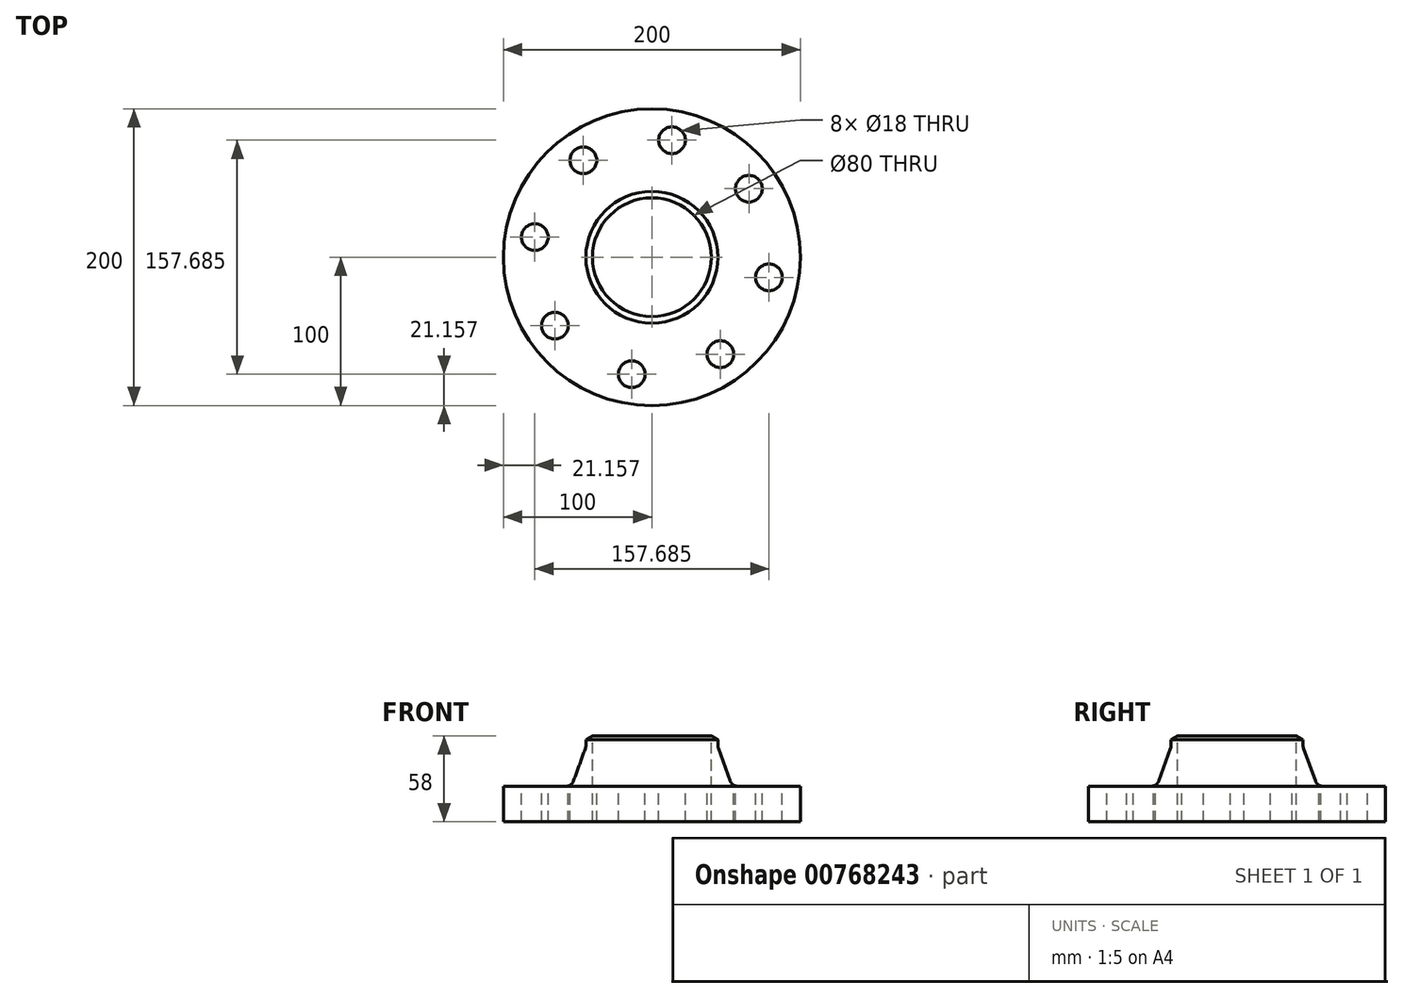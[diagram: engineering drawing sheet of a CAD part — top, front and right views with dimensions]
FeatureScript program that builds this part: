
annotation { "Feature Type Name" : "Feature", "Feature Type Description" : "" }
export const myFeature = defineFeature(function(context is Context, id is Id, definition is map)
    precondition{}
    {
        {
            var Q0;
            Q0=qCreatedBy(makeId("Front.planeOp"),FACE);
            var sketch = newSketch(context, id + "F0", { "sketchPlane" : qUnion([Q0])});
            skLineSegment(sketch, "E0", {"start": v(0, 94.05) * mm, "end": v(0, -88.04) * mm, "construction": true});
            skLineSegment(sketch, "E1", {"start": v(-40, 0) * mm, "end": v(-40, 58) * mm});
            skLineSegment(sketch, "E2", {"start": v(-40, 58) * mm, "end": v(-44.45, 55.43) * mm});
            skLineSegment(sketch, "E3", {"start": v(-54.07, 24) * mm, "end": v(-100, 24) * mm});
            skLineSegment(sketch, "E4", {"start": v(-100, 24) * mm, "end": v(-100, 0) * mm});
            skLineSegment(sketch, "E5", {"start": v(-100, 0) * mm, "end": v(-40, 0) * mm});
            skLineSegment(sketch, "E6", {"start": v(-44.45, 55.43) * mm, "end": v(-44.45, 50.43) * mm});
            skLineSegment(sketch, "E7", {"start": v(-44.45, 50.43) * mm, "end": v(-54.07, 24) * mm});
            skSolve(sketch);
        }
        {
            var Q0;
            Q0=makeQuery(id+"F0.imprint","IMPRINT",FACE,{"disambiguationData":[TD([[makeQuery(id+"F0.imprint","IMPRINT",EDGE,{"derivedFrom":sQuery(id+"F0.wireOp",EDGE,"E1")}),1.0]])]});
            var Q1;
            Q1=sQuery(id+"F0.wireOp",EDGE,"E0");
            revolve(context, id + "F1", {"surfaceOperationType" : NewSurfaceOperationType.NEW, "entities" : qUnion([Q0]), "axis" : qUnion([Q1]), "revolveType" : RevolveType.FULL});
        }
        {
            var Q0;
            Q0=makeQuery(id+"F1.opRevolve","SWEPT_FACE",FACE,{"disambiguationData":[OSD([sQuery(id+"F0.wireOp",EDGE,"E3")])]});
            var sketch = newSketch(context, id + "F2", { "sketchPlane" : qUnion([Q0])});
            skCircle(sketch, "E8", {"center": v(0, 0) * mm, "radius": 80 * mm, "construction": true});
            skCircle(sketch, "E9", {"center": v(-46.16, 65.34) * mm, "radius": 9 * mm});
            skCircle(sketch, "E10.1.0", {"center": v(-78.84, 13.56) * mm, "radius": 9 * mm});
            skCircle(sketch, "E10.2.0", {"center": v(-65.34, -46.16) * mm, "radius": 9 * mm});
            skCircle(sketch, "E10.3.0", {"center": v(-13.56, -78.84) * mm, "radius": 9 * mm});
            skCircle(sketch, "E10.4.0", {"center": v(46.16, -65.34) * mm, "radius": 9 * mm});
            skCircle(sketch, "E10.5.0", {"center": v(78.84, -13.56) * mm, "radius": 9 * mm});
            skCircle(sketch, "E10.6.0", {"center": v(65.34, 46.16) * mm, "radius": 9 * mm});
            skCircle(sketch, "E10.7.0", {"center": v(13.56, 78.84) * mm, "radius": 9 * mm});
            skSolve(sketch);
        }
        {
            var Q0;
            Q0=qSketchRegion(id+"F2",true);
            extrude(context, id + "F3", {"entities" : qUnion([Q0]), "operationType" : NewBodyOperationType.REMOVE, "oppositeDirection" : true, "depth" : 25 * mm, "offsetDistance" : 25 * mm});
        }
        {
            var Q0;
            Q0=makeQuery(id+"F1.opRevolve","SWEPT_EDGE",EDGE,{"disambiguationData":[OSD([sQuery(id+"F0.wireOp",EDGE,"E3"),sQuery(id+"F0.wireOp",EDGE,"E7")])]});
            var Q1;
            Q1=makeQuery(id+"F1.opRevolve","SWEPT_EDGE",EDGE,{"disambiguationData":[OSD([sQuery(id+"F0.wireOp",EDGE,"E6"),sQuery(id+"F0.wireOp",EDGE,"E7")])]});
            fillet(context, id + "F4", {"entities" : qUnion([Q0, Q1]), "radius" : 5 * mm, "tangentPropagation" : true, "allowEdgeOverflow" : false});
        }
    });
